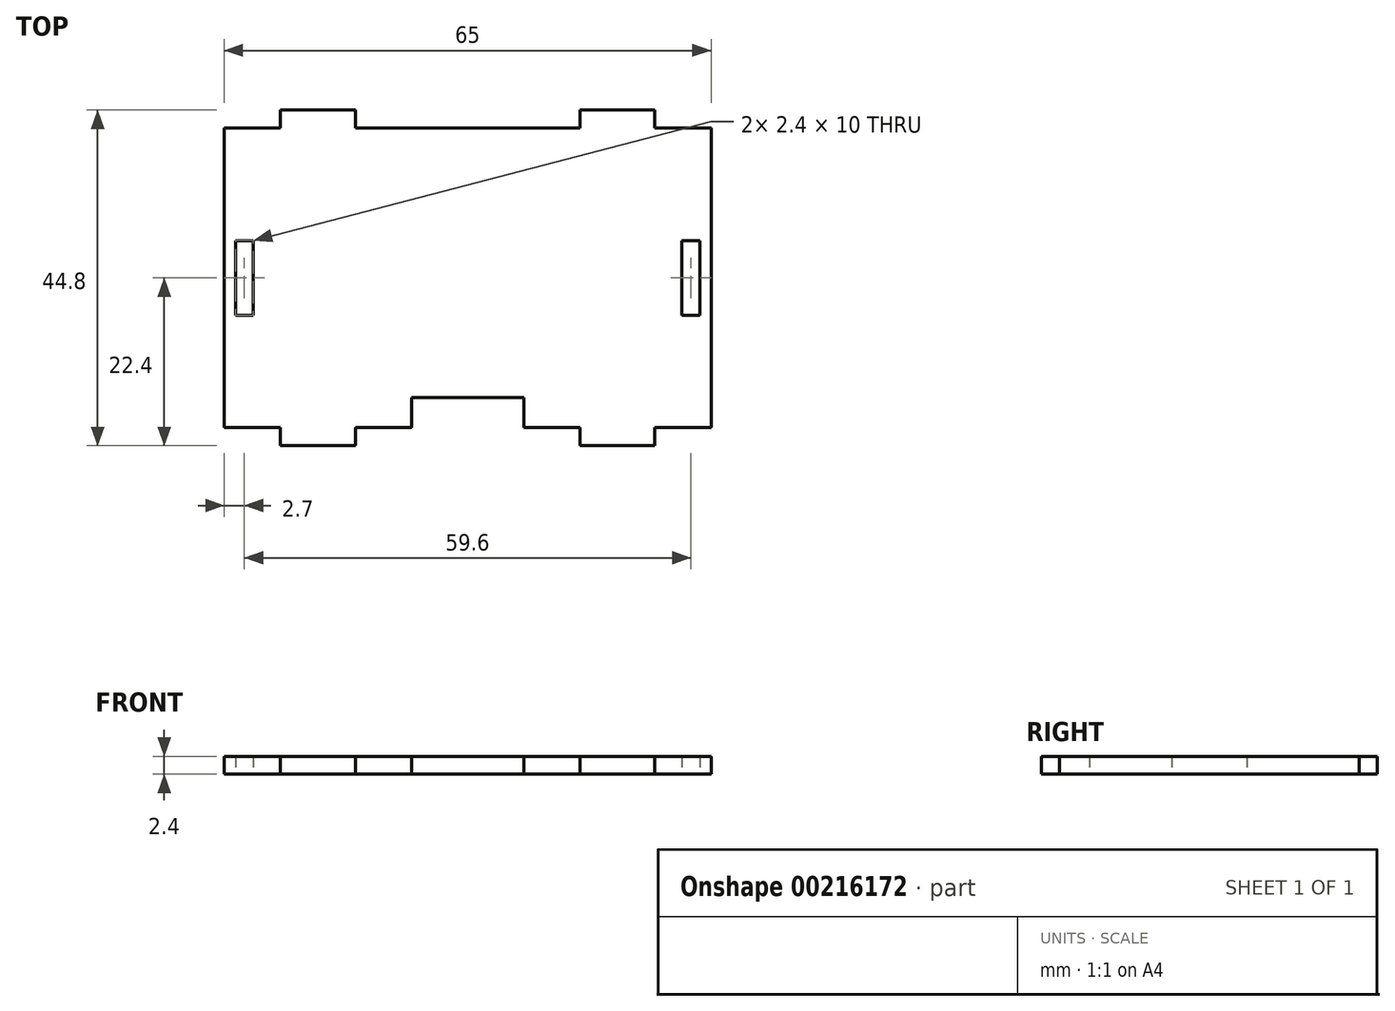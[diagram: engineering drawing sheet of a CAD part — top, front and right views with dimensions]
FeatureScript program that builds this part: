
annotation { "Feature Type Name" : "Feature", "Feature Type Description" : "" }
export const myFeature = defineFeature(function(context is Context, id is Id, definition is map)
    precondition{}
    {
        {
            var Q0;
            Q0=qCreatedBy(makeId("Top.planeOp"),FACE);
            var sketch = newSketch(context, id + "F0", { "sketchPlane" : qUnion([Q0])});
            skLineSegment(sketch, "E0.bottom", {"start": v(32.5, 20) * mm, "end": v(25, 20) * mm});
            skLineSegment(sketch, "E0.top", {"start": v(32.5, -20) * mm, "end": v(25, -20) * mm});
            skLineSegment(sketch, "E0.left", {"start": v(32.5, 20) * mm, "end": v(32.5, -20) * mm});
            skLineSegment(sketch, "E0.right", {"start": v(-32.5, 20) * mm, "end": v(-32.5, -20) * mm});
            skPoint(sketch, "E0.middle", {"position": v(0, 0) * mm});
            skLineSegment(sketch, "E1.bottom", {"start": v(-15, 22.4) * mm, "end": v(-25, 22.4) * mm});
            skLineSegment(sketch, "E1.left", {"start": v(-15, 22.4) * mm, "end": v(-15, 20) * mm});
            skLineSegment(sketch, "E1.right", {"start": v(-25, 22.4) * mm, "end": v(-25, 20) * mm});
            skPoint(sketch, "E1.middle", {"position": v(-20, 20) * mm});
            skLineSegment(sketch, "E2.bottom", {"start": v(25, 22.4) * mm, "end": v(15, 22.4) * mm});
            skLineSegment(sketch, "E2.left", {"start": v(25, 22.4) * mm, "end": v(25, 20) * mm});
            skLineSegment(sketch, "E2.right", {"start": v(15, 22.4) * mm, "end": v(15, 20) * mm});
            skPoint(sketch, "E2.middle", {"position": v(20, 20) * mm});
            skLineSegment(sketch, "E3.top", {"start": v(-15, -22.4) * mm, "end": v(-25, -22.4) * mm});
            skLineSegment(sketch, "E3.left", {"start": v(-15, -20) * mm, "end": v(-15, -22.4) * mm});
            skLineSegment(sketch, "E3.right", {"start": v(-25, -20) * mm, "end": v(-25, -22.4) * mm});
            skPoint(sketch, "E3.middle", {"position": v(-20, -20) * mm});
            skLineSegment(sketch, "E4.top", {"start": v(25, -22.4) * mm, "end": v(15, -22.4) * mm});
            skLineSegment(sketch, "E4.left", {"start": v(25, -20) * mm, "end": v(25, -22.4) * mm});
            skLineSegment(sketch, "E4.right", {"start": v(15, -20) * mm, "end": v(15, -22.4) * mm});
            skPoint(sketch, "E4.middle", {"position": v(20, -20) * mm});
            skLineSegment(sketch, "E5.bottom", {"start": v(7.5, -16) * mm, "end": v(-7.5, -16) * mm});
            skLineSegment(sketch, "E5.left", {"start": v(7.5, -16) * mm, "end": v(7.5, -20) * mm});
            skLineSegment(sketch, "E5.right", {"start": v(-7.5, -16) * mm, "end": v(-7.5, -20) * mm});
            skPoint(sketch, "E5.middle", {"position": v(0, -20) * mm});
            skPoint(sketch, "E6.orphan", {"position": v(-25, 17.6) * mm});
            skPoint(sketch, "E7.orphan", {"position": v(-15, 17.6) * mm});
            skLineSegment(sketch, "E8.trimOffspring", {"start": v(-25, 20) * mm, "end": v(-32.5, 20) * mm});
            skLineSegment(sketch, "E9.trimOffspring", {"start": v(15, 20) * mm, "end": v(-15, 20) * mm});
            skPoint(sketch, "E2.top.end.orphan", {"position": v(15, 17.6) * mm});
            skPoint(sketch, "E10.orphan", {"position": v(25, 17.6) * mm});
            skPoint(sketch, "E11.orphan", {"position": v(15, -17.6) * mm});
            skLineSegment(sketch, "E12.trimOffspring", {"start": v(15, -20) * mm, "end": v(7.5, -20) * mm});
            skPoint(sketch, "E13.orphan", {"position": v(25, -17.6) * mm});
            skLineSegment(sketch, "E14.trimOffspring", {"start": v(-7.5, -20) * mm, "end": v(-15, -20) * mm});
            skPoint(sketch, "E5.top.start.orphan", {"position": v(7.5, -24) * mm});
            skPoint(sketch, "E15.orphan", {"position": v(-7.5, -24) * mm});
            skPoint(sketch, "E16.orphan", {"position": v(-25, -17.6) * mm});
            skPoint(sketch, "E17.orphan", {"position": v(-15, -17.6) * mm});
            skLineSegment(sketch, "E18.trimOffspring", {"start": v(-25, -20) * mm, "end": v(-32.5, -20) * mm});
            skLineSegment(sketch, "E19.bottom", {"start": v(-28.6, 5) * mm, "end": v(-31, 5) * mm});
            skLineSegment(sketch, "E19.top", {"start": v(-28.6, -5) * mm, "end": v(-31, -5) * mm});
            skLineSegment(sketch, "E19.left", {"start": v(-28.6, 5) * mm, "end": v(-28.6, -5) * mm});
            skLineSegment(sketch, "E19.right", {"start": v(-31, 5) * mm, "end": v(-31, -5) * mm});
            skPoint(sketch, "E19.middle", {"position": v(-29.8, 0) * mm});
            skLineSegment(sketch, "E20.bottom", {"start": v(31, 5) * mm, "end": v(28.6, 5) * mm});
            skLineSegment(sketch, "E20.top", {"start": v(31, -5) * mm, "end": v(28.6, -5) * mm});
            skLineSegment(sketch, "E20.left", {"start": v(31, 5) * mm, "end": v(31, -5) * mm});
            skLineSegment(sketch, "E20.right", {"start": v(28.6, 5) * mm, "end": v(28.6, -5) * mm});
            skPoint(sketch, "E20.middle", {"position": v(29.8, 0) * mm});
            skSolve(sketch);
        }
        {
            var Q0;
            Q0=qSketchRegion(id+"F0",true);
            extrude(context, id + "F1", {"entities" : qUnion([Q0]), "depth" : 2.4 * mm});
        }
    });
